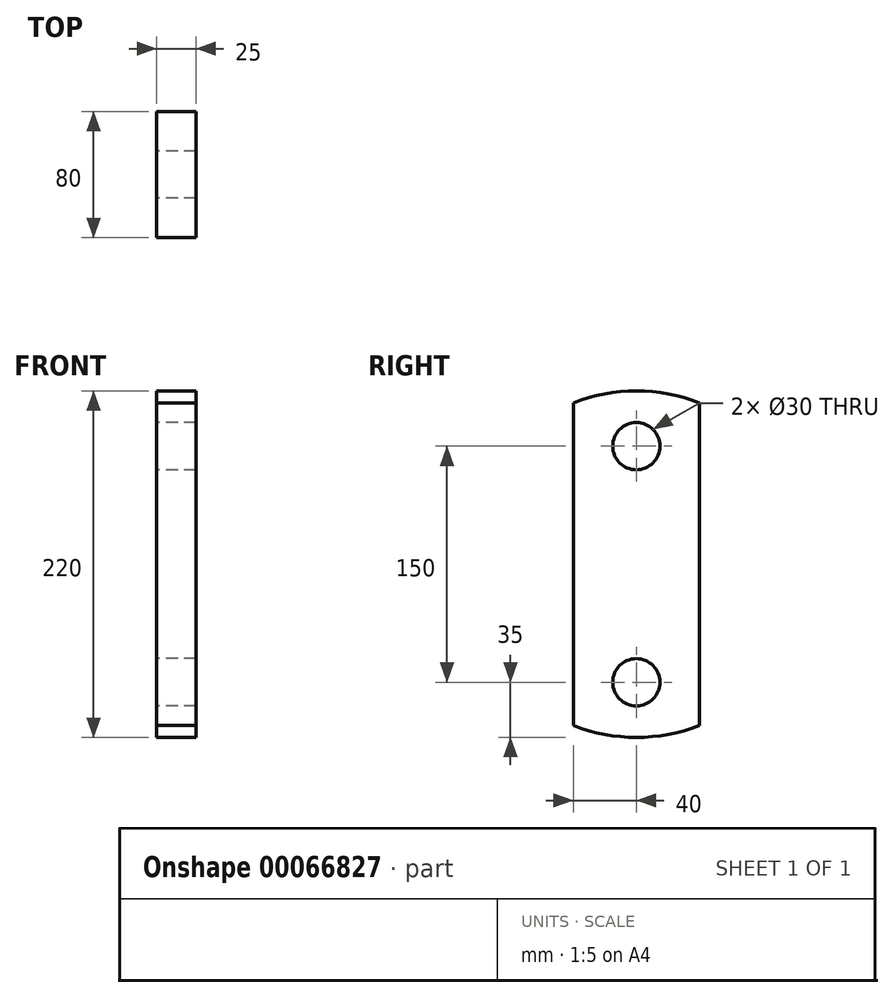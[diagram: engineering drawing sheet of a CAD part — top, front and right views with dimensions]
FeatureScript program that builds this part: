
annotation { "Feature Type Name" : "Feature", "Feature Type Description" : "" }
export const myFeature = defineFeature(function(context is Context, id is Id, definition is map)
    precondition{}
    {
        {
            var Q0;
            Q0=qCreatedBy(makeId("Right.planeOp"),FACE);
            var sketch = newSketch(context, id + "F0", { "sketchPlane" : qUnion([Q0])});
            skArc(sketch, "E0", {"start": v(-40, -102.47) * mm, "mid": v(0, -110) * mm, "end": v(40, -102.47) * mm});
            skLineSegment(sketch, "E1", {"start": v(-40, 102.47) * mm, "end": v(-40, -102.47) * mm});
            skLineSegment(sketch, "E2", {"start": v(40, 102.47) * mm, "end": v(40, -102.47) * mm});
            skArc(sketch, "E3.trimOffspring", {"start": v(40, 102.47) * mm, "mid": v(0, 110) * mm, "end": v(-40, 102.47) * mm});
            skCircle(sketch, "E4", {"center": v(0, 75) * mm, "radius": 15 * mm});
            skCircle(sketch, "E5", {"center": v(0, -75) * mm, "radius": 15 * mm});
            skSolve(sketch);
        }
        {
            var Q0;
            Q0=makeQuery(id+"F0.imprint","IMPRINT",FACE,{"disambiguationData":[TD([[makeQuery(id+"F0.imprint","IMPRINT",EDGE,{"derivedFrom":sQuery(id+"F0.wireOp",EDGE,"E0")}),1.0]])]});
            extrude(context, id + "F1", {"entities" : qUnion([Q0]), "depth" : 25 * mm});
        }
    });
